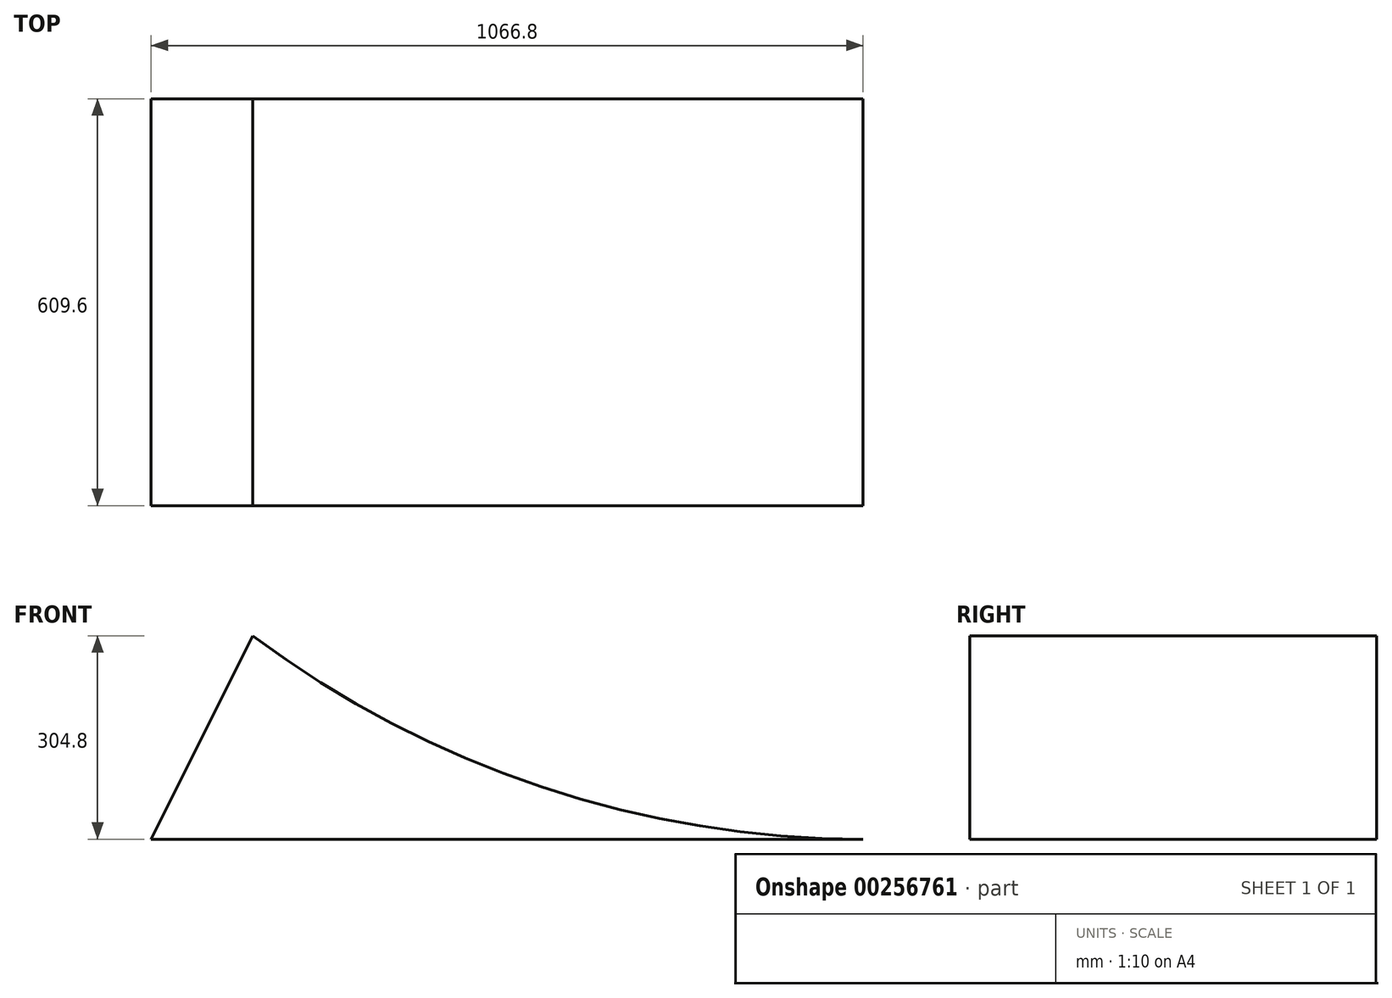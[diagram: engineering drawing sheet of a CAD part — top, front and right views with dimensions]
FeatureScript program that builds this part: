
annotation { "Feature Type Name" : "Feature", "Feature Type Description" : "" }
export const myFeature = defineFeature(function(context is Context, id is Id, definition is map)
    precondition{}
    {
        {
            var Q0;
            Q0=qCreatedBy(makeId("Front.planeOp"),FACE);
            var sketch = newSketch(context, id + "F0", { "sketchPlane" : qUnion([Q0])});
            skLineSegment(sketch, "E0.bottom", {"start": v(-533.4, 152.4) * mm, "end": v(533.4, 152.4) * mm});
            skLineSegment(sketch, "E0.top", {"start": v(-533.4, -152.4) * mm, "end": v(533.4, -152.4) * mm});
            skLineSegment(sketch, "E0.left", {"start": v(-533.4, 152.4) * mm, "end": v(-533.4, -152.4) * mm});
            skLineSegment(sketch, "E0.right", {"start": v(533.4, 152.4) * mm, "end": v(533.4, -152.4) * mm});
            skPoint(sketch, "E0.middle", {"position": v(0, 0) * mm});
            skLineSegment(sketch, "E1", {"start": v(-381, 152.4) * mm, "end": v(-381, -152.4) * mm, "construction": true});
            skLineSegment(sketch, "E2", {"start": v(-381, 152.4) * mm, "end": v(-533.4, -152.4) * mm});
            skArc(sketch, "E3", {"start": v(-381, 152.4) * mm, "mid": v(51.47, -74.2) * mm, "end": v(533.4, -152.4) * mm});
            skSolve(sketch);
        }
        {
            var Q0;
            Q0=makeQuery(id+"F0.imprint","IMPRINT",FACE,{"disambiguationData":[TD([[makeQuery(id+"F0.imprint","IMPRINT",EDGE,{"derivedFrom":sQuery(id+"F0.wireOp",EDGE,"E0.top")}),1.0]])]});
            extrude(context, id + "F1", {"entities" : qUnion([Q0]), "depth" : 609.6 * mm, "symmetric" : true});
        }
    });
